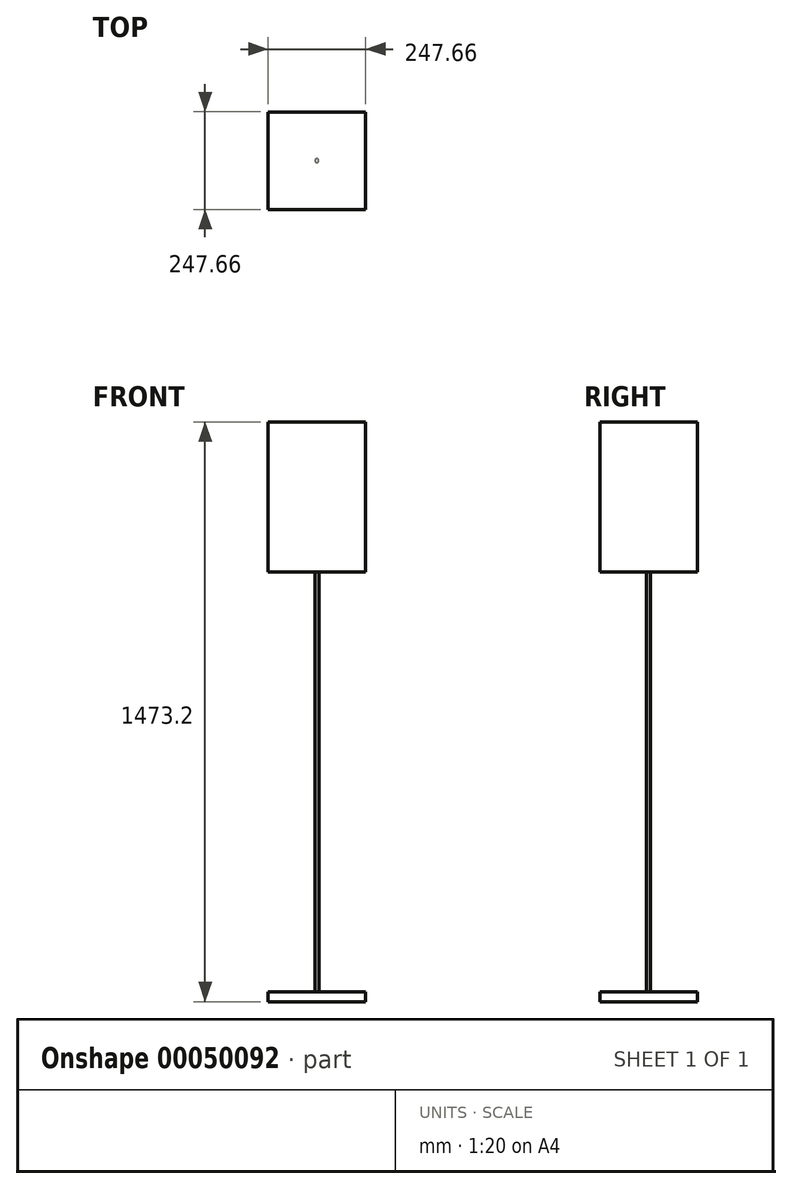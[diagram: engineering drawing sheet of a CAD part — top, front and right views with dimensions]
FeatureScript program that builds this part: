
annotation { "Feature Type Name" : "Feature", "Feature Type Description" : "" }
export const myFeature = defineFeature(function(context is Context, id is Id, definition is map)
    precondition{}
    {
        {
            var Q0;
            Q0=qCreatedBy(makeId("Top.planeOp"),FACE);
            var sketch = newSketch(context, id + "F0", { "sketchPlane" : qUnion([Q0])});
            skLineSegment(sketch, "E0.bottom", {"start": v(-123.83, 123.83) * mm, "end": v(123.83, 123.83) * mm});
            skLineSegment(sketch, "E0.top", {"start": v(-123.83, -123.83) * mm, "end": v(123.83, -123.83) * mm});
            skLineSegment(sketch, "E0.left", {"start": v(-123.83, 123.83) * mm, "end": v(-123.83, -123.83) * mm});
            skLineSegment(sketch, "E0.right", {"start": v(123.83, 123.83) * mm, "end": v(123.83, -123.83) * mm});
            skSolve(sketch);
        }
        {
            var Q0;
            Q0 = qSketchRegion(id + "F0", true);
            extrude(context, id + "F1", {"entities" : qUnion([Q0]), "depth" : 25.4 * mm});
        }
        {
            var Q0;
            Q0=makeQuery(id+"F1.opExtrude","CAP_FACE",FACE,{"disambiguationData":[OSD([sQuery(id+"F0.wireOp",EDGE,"E0.bottom"),sQuery(id+"F0.wireOp",EDGE,"E0.top"),sQuery(id+"F0.wireOp",EDGE,"E0.left"),sQuery(id+"F0.wireOp",EDGE,"E0.right")])],"isStart":false});
            var sketch = newSketch(context, id + "F2", { "sketchPlane" : qUnion([Q0])});
            skCircle(sketch, "E1", {"center": v(0, 0) * mm, "radius": 4.76 * mm});
            skSolve(sketch);
        }
        {
            var Q0;
            Q0 = qSketchRegion(id + "F2", true);
            extrude(context, id + "F3", {"entities" : qUnion([Q0]), "operationType" : NewBodyOperationType.ADD, "depth" : 1066.8 * mm});
        }
        {
            var Q0;
            Q0=makeQuery(id+"F3.opExtrude","CAP_FACE",FACE,{"disambiguationData":[OSD([sQuery(id+"F2.wireOp",EDGE,"E1")])],"isStart":false});
            var sketch = newSketch(context, id + "F4", { "sketchPlane" : qUnion([Q0])});
            skLineSegment(sketch, "E2.bottom", {"start": v(-123.83, 123.83) * mm, "end": v(123.83, 123.83) * mm});
            skLineSegment(sketch, "E2.top", {"start": v(-123.83, -123.83) * mm, "end": v(123.83, -123.83) * mm});
            skLineSegment(sketch, "E2.left", {"start": v(-123.83, 123.83) * mm, "end": v(-123.83, -123.83) * mm});
            skLineSegment(sketch, "E2.right", {"start": v(123.83, 123.83) * mm, "end": v(123.83, -123.83) * mm});
            skSolve(sketch);
        }
        {
            var Q0;
            Q0 = qSketchRegion(id + "F4", true);
            extrude(context, id + "F5", {"entities" : qUnion([Q0]), "operationType" : NewBodyOperationType.ADD, "depth" : 381 * mm});
        }
    });
